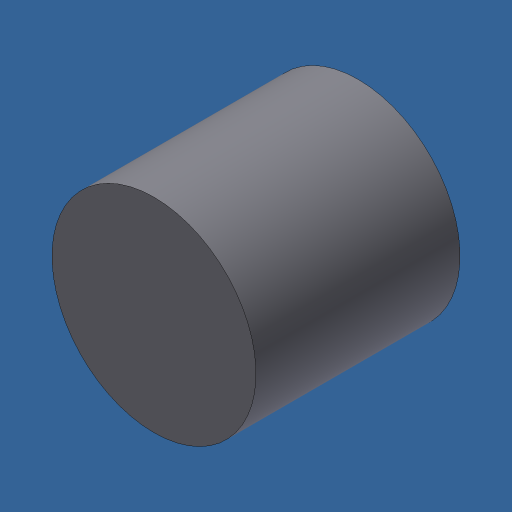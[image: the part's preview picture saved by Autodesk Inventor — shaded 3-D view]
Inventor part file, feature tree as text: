
AUTODESK INVENTOR PART (.ipt)
format: ipt  version: 2024.3 (Build 283343000, 343)  size: 113,664 bytes
history: native  units: mm
features: other x1, revolve x1
ambient origin geometry x8: Origin, YZ Plane, XZ Plane, XY Plane, X Axis, Y Axis, Z Axis, Center Point
bodies: Body1 (feature_tree)
feature tree (2):
  other  "Finish - None"
  revolve  "Revolution1"  [1 undecoded]
note: 1 required parameter value undecoded (feature->parameter linkage not recoverable at this tier; creation-order binding heuristic only, values carry confidence <= 0.55)
